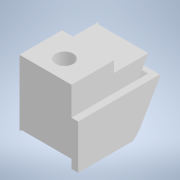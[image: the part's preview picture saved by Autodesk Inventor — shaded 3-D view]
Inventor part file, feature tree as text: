
AUTODESK INVENTOR PART (.ipt)
format: ipt  version: 2022 (Build 260153000, 153)  size: 284,672 bytes
history: native  units: mm
features: other x8, sketch x8, extrude x8, reference x7, projected_geometry x6, fillet x3
ambient origin geometry x8: Origin, YZ Plane, XZ Plane, XY Plane, X Axis, Y Axis, Z Axis, Center Point
bodies: Body1 (feature_tree)
feature tree (40):
  other  "Твердое тело1"
  sketch  "Эскиз1"
  other  "РабПлоскость1"
  extrude  "Выдавливание1"  Depth=6.0mm
  extrude  "Выдавливание2"  Depth=0.3mm
  extrude  "Выдавливание3"  Depth=10.0mm TaperAngle=0.0deg
  extrude  "Выдавливание4"  Depth=0.2mm
  extrude  "Выдавливание5"  Depth=2.0mm TaperAngle=0.0deg
  extrude  "Выдавливание6"  Depth=5.0mm
  fillet  "Сопряжение1"  Radius=10.0mm
  extrude  "Выдавливание7"  Depth=3.2mm
  fillet  "Сопряжение2"  Radius=5.5mm
  fillet  "Сопряжение3"  Radius=3.4mm
  extrude  "Выдавливание8"  Depth=0.15mm
  reference  "Ссылка1"
  reference  "Ссылка2"
  reference  "Ссылка3"
  reference  "Ссылка4"
  sketch  "Эскиз2"
  projected_geometry  "Спроецированная петля1"
  reference  "Ссылка5"
  sketch  "Эскиз3"
  sketch  "Эскиз4"
  sketch  "Эскиз5"
  reference  "Ссылка6"
  projected_geometry  "Спроецированная петля2"
  reference  "Ссылка7"
  sketch  "Эскиз6"
  projected_geometry  "Спроецированная петля3"
  projected_geometry  "Спроецированная петля4"
  sketch  "Эскиз7"
  projected_geometry  "Спроецированная петля5"
  sketch  "Эскиз8"
  projected_geometry  "Спроецированная петля6"
  other  "<userpath>\Documents\Git\MZCAT_2024\MZCAT_4.iam"
  other  "MZCAT_4.iam"
  other  "base:1"
  other  "CAT_protector:1"
  other  "motherboard_plate:1"
  other  "commutationCATboard:1"
